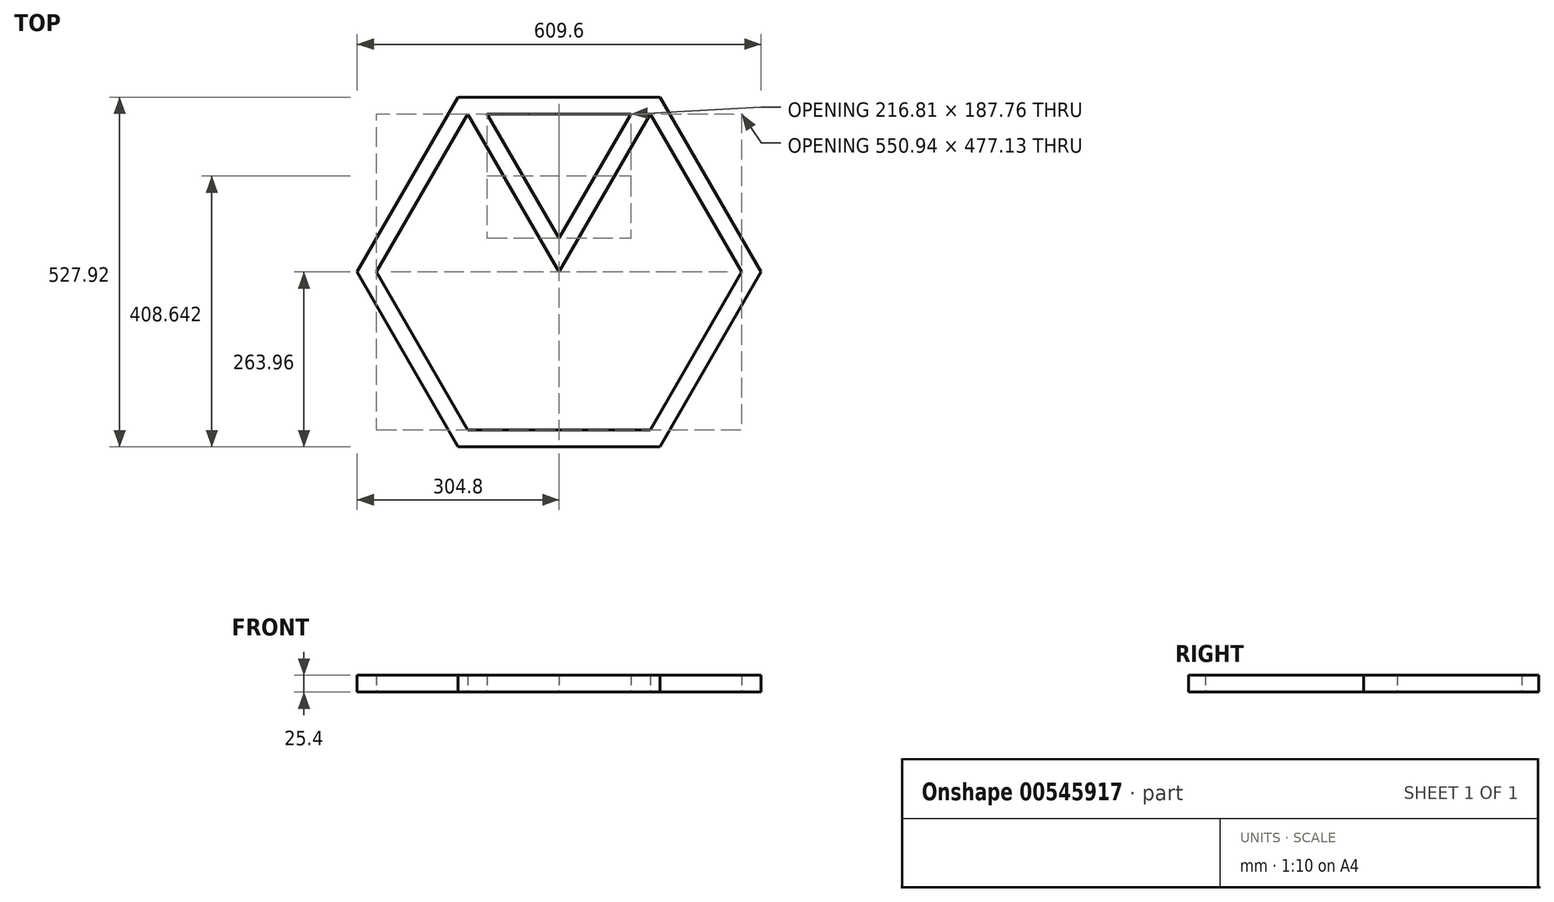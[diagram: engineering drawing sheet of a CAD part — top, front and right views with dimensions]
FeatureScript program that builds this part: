
annotation { "Feature Type Name" : "Feature", "Feature Type Description" : "" }
export const myFeature = defineFeature(function(context is Context, id is Id, definition is map)
    precondition{}
    {
        {
            var Q0;
            Q0=qCreatedBy(makeId("Top.planeOp"),FACE);
            var sketch = newSketch(context, id + "F0", { "sketchPlane" : qUnion([Q0])});
            skCircle(sketch, "E0.cCircle", {"center": v(0, 0) * mm, "radius": 263.96 * mm, "construction": true});
            skLineSegment(sketch, "E0.0", {"start": v(-152.4, 263.96) * mm, "end": v(152.4, 263.96) * mm});
            skLineSegment(sketch, "E0.1", {"start": v(152.4, 263.96) * mm, "end": v(304.8, 0) * mm});
            skLineSegment(sketch, "E0.2", {"start": v(304.8, 0) * mm, "end": v(152.4, -263.96) * mm});
            skLineSegment(sketch, "E0.3", {"start": v(152.4, -263.96) * mm, "end": v(-152.4, -263.96) * mm});
            skLineSegment(sketch, "E0.4", {"start": v(-152.4, -263.96) * mm, "end": v(-304.8, 0) * mm});
            skLineSegment(sketch, "E0.5", {"start": v(-304.8, 0) * mm, "end": v(-152.4, 263.96) * mm});
            skPoint(sketch, "E0.0.midPoint", {"position": v(0, 263.96) * mm});
            skLineSegment(sketch, "E1.0", {"start": v(-275.47, 0) * mm, "end": v(-137.74, 238.56) * mm});
            skLineSegment(sketch, "E1.1", {"start": v(137.74, 238.56) * mm, "end": v(275.47, 0) * mm});
            skLineSegment(sketch, "E1.2", {"start": v(275.47, 0) * mm, "end": v(137.74, -238.56) * mm});
            skLineSegment(sketch, "E1.3", {"start": v(-108.4, 238.56) * mm, "end": v(108.4, 238.56) * mm});
            skLineSegment(sketch, "E1.4", {"start": v(137.74, -238.56) * mm, "end": v(-137.74, -238.56) * mm});
            skLineSegment(sketch, "E1.5", {"start": v(-137.74, -238.56) * mm, "end": v(-275.47, 0) * mm});
            skLineSegment(sketch, "E2", {"start": v(0, 0) * mm, "end": v(-137.74, 238.56) * mm});
            skLineSegment(sketch, "E3", {"start": v(0, 0) * mm, "end": v(137.74, 238.56) * mm});
            skLineSegment(sketch, "E4.0", {"start": v(0, 50.8) * mm, "end": v(-108.4, 238.56) * mm});
            skLineSegment(sketch, "E4.1", {"start": v(0, 50.8) * mm, "end": v(108.4, 238.56) * mm});
            skSolve(sketch);
        }
        {
            var Q0;
            Q0=makeQuery(id+"F0.imprint","IMPRINT",FACE,{"disambiguationData":[TD([[makeQuery(id+"F0.imprint","IMPRINT",EDGE,{"derivedFrom":sQuery(id+"F0.wireOp",EDGE,"E0.0")}),-1.0]])]});
            extrude(context, id + "F1", {"entities" : qUnion([Q0]), "depth" : 25.4 * mm, "offsetDistance" : 25.4 * mm});
        }
    });
